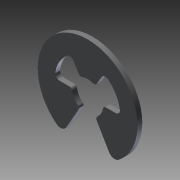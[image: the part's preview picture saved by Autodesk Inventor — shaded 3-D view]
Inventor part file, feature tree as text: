
AUTODESK INVENTOR PART (.ipt)
format: ipt  version: 2012 (Build 160160000, 160)  size: 115,200 bytes
history: native  units: in
note: dims shown in document units (in); Inventor stores cm internally (conversion verified against a paired STEP export)
features: other x7, extrude x1, sketch x1
ambient origin geometry x8: Origin, YZ Plane, XZ Plane, XY Plane, X Axis, Y Axis, Z Axis, Center Point
bodies: Solid1 (feature_tree)
feature tree (9):
  extrude  "Extrusion1"  [1 undecoded]
  other  "RR_XY"
  other  "RR_YZ"
  other  "RR_ZX"
  other  "RR_X"
  other  "RR_Y"
  other  "RR_Z"
  other  "RR_Center"
  sketch  "Sketch_1"  dims[d0=0.015in d1=0.0in]
note: 1 required parameter value undecoded (feature->parameter linkage not recoverable at this tier; creation-order binding heuristic only, values carry confidence <= 0.55)
